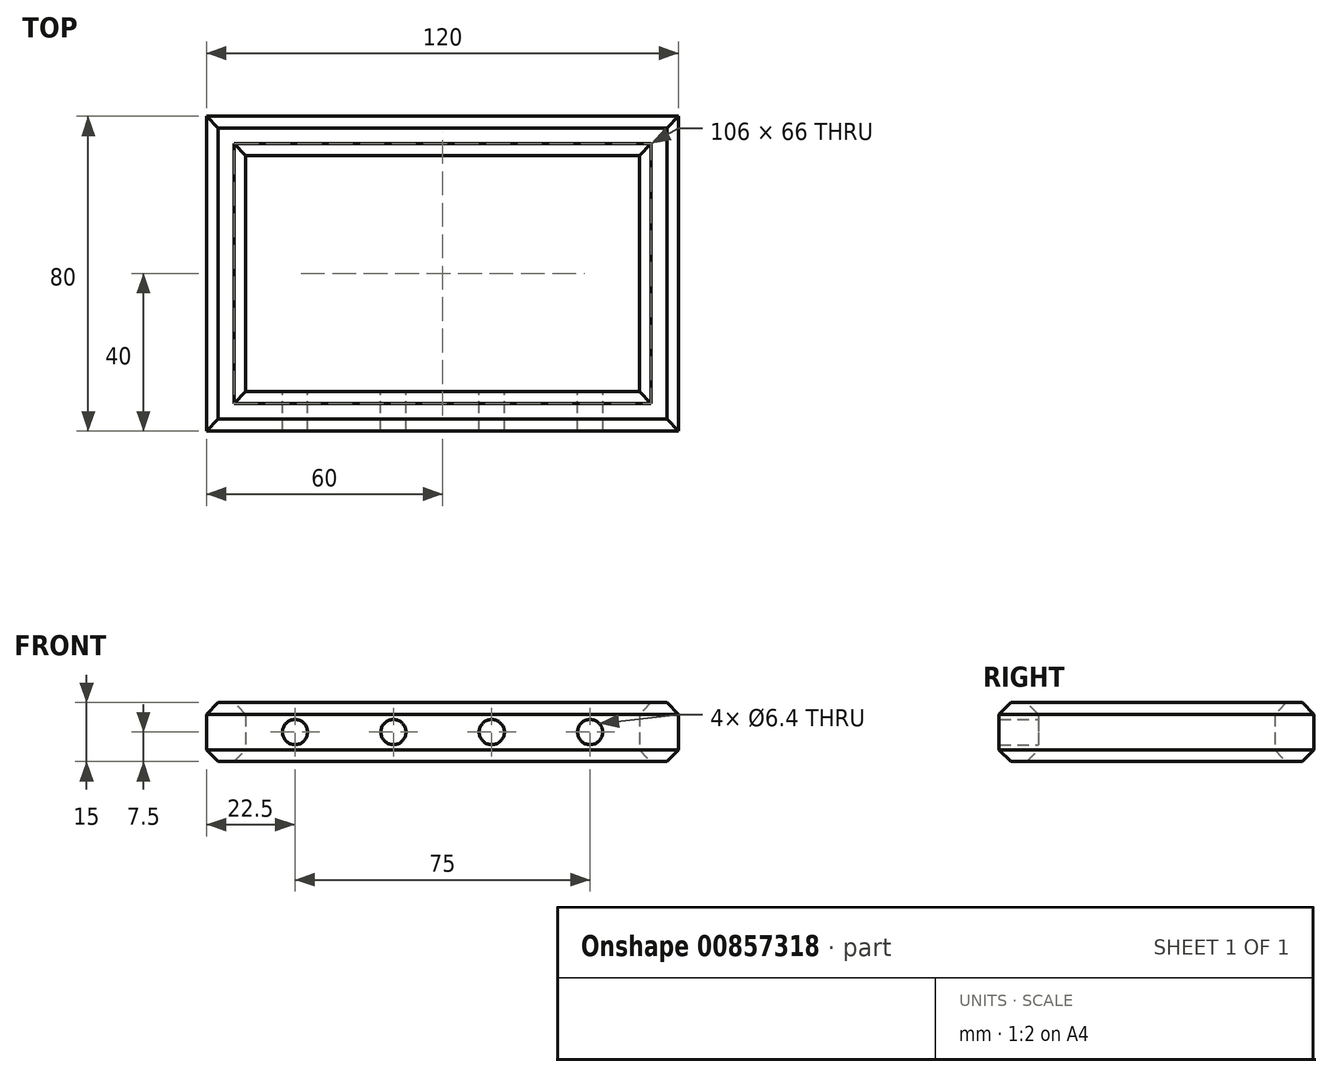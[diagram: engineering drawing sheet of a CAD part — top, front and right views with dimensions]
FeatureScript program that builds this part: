
annotation { "Feature Type Name" : "Feature", "Feature Type Description" : "" }
export const myFeature = defineFeature(function(context is Context, id is Id, definition is map)
    precondition{}
    {
        {
            var Q0;
            Q0=qCreatedBy(makeId("Top.planeOp"),FACE);
            var sketch = newSketch(context, id + "F0", { "sketchPlane" : qUnion([Q0])});
            skLineSegment(sketch, "E0", {"start": v(0, 0) * mm, "end": v(-53.05, 0) * mm, "construction": true});
            skLineSegment(sketch, "E1", {"start": v(0, 0) * mm, "end": v(0, 23.05) * mm, "construction": true});
            skLineSegment(sketch, "E2", {"start": v(0, 0) * mm, "end": v(9.55, 0) * mm, "construction": true});
            skLineSegment(sketch, "E3", {"start": v(0, 0) * mm, "end": v(0, -12.76) * mm, "construction": true});
            skLineSegment(sketch, "E4.bottom", {"start": v(0, 0) * mm, "end": v(-120, 0) * mm});
            skLineSegment(sketch, "E4.top", {"start": v(0, 80) * mm, "end": v(-120, 80) * mm});
            skLineSegment(sketch, "E4.left", {"start": v(0, 0) * mm, "end": v(0, 80) * mm});
            skLineSegment(sketch, "E4.right", {"start": v(-120, 0) * mm, "end": v(-120, 80) * mm});
            skLineSegment(sketch, "E5.bottom", {"start": v(-10, 10) * mm, "end": v(-110, 10) * mm});
            skLineSegment(sketch, "E5.top", {"start": v(-10, 70) * mm, "end": v(-110, 70) * mm});
            skLineSegment(sketch, "E5.left", {"start": v(-10, 10) * mm, "end": v(-10, 70) * mm});
            skLineSegment(sketch, "E5.right", {"start": v(-110, 10) * mm, "end": v(-110, 70) * mm});
            skSolve(sketch);
        }
        {
            var Q0;
            Q0=makeQuery(id+"F0.imprint","IMPRINT",FACE,{"disambiguationData":[TD([[makeQuery(id+"F0.imprint","IMPRINT",EDGE,{"derivedFrom":sQuery(id+"F0.wireOp",EDGE,"E4.bottom")}),-1.0]])]});
            extrude(context, id + "F1", {"entities" : qUnion([Q0]), "depth" : 15 * mm, "offsetDistance" : 25 * mm});
        }
        {
            var Q0;
            Q0=makeQuery(id+"F1.opExtrude","SWEPT_FACE",FACE,{"disambiguationData":[OSD([sQuery(id+"F0.wireOp",EDGE,"E5.bottom")])]});
            var sketch = newSketch(context, id + "F2", { "sketchPlane" : qUnion([Q0])});
            skCircle(sketch, "E6", {"center": v(72.5, 7.5) * mm, "radius": 3.2 * mm});
            skCircle(sketch, "E7", {"center": v(47.5, 7.5) * mm, "radius": 3.2 * mm});
            skLineSegment(sketch, "E8", {"start": v(74.14, 7.5) * mm, "end": v(32.95, 7.5) * mm, "construction": true});
            skLineSegment(sketch, "E9", {"start": v(60, 10.85) * mm, "end": v(60, 4.57) * mm, "construction": true});
            skCircle(sketch, "E10", {"center": v(97.5, 7.5) * mm, "radius": 3.2 * mm});
            skCircle(sketch, "E11", {"center": v(22.5, 7.5) * mm, "radius": 3.2 * mm});
            skSolve(sketch);
        }
        {
            var Q0;
            Q0=makeQuery(id+"F2.imprint","IMPRINT",FACE,{"disambiguationData":[TD([[makeQuery(id+"F2.imprint","IMPRINT",EDGE,{"derivedFrom":sQuery(id+"F2.wireOp",EDGE,"E6")}),1.0]])]});
            var Q1;
            Q1=makeQuery(id+"F2.imprint","IMPRINT",FACE,{"disambiguationData":[TD([[makeQuery(id+"F2.imprint","IMPRINT",EDGE,{"derivedFrom":sQuery(id+"F2.wireOp",EDGE,"E7")}),1.0]])]});
            var Q2;
            Q2=makeQuery(id+"F2.imprint","IMPRINT",FACE,{"disambiguationData":[TD([[makeQuery(id+"F2.imprint","IMPRINT",EDGE,{"derivedFrom":sQuery(id+"F2.wireOp",EDGE,"E10")}),1.0]])]});
            var Q3;
            Q3=makeQuery(id+"F2.imprint","IMPRINT",FACE,{"disambiguationData":[TD([[makeQuery(id+"F2.imprint","IMPRINT",EDGE,{"derivedFrom":sQuery(id+"F2.wireOp",EDGE,"E11")}),1.0]])]});
            extrude(context, id + "F3", {"entities" : qUnion([Q0, Q1, Q2, Q3]), "operationType" : NewBodyOperationType.REMOVE, "endBound" : BoundingType.THROUGH_ALL, "oppositeDirection" : true, "depth" : 25 * mm, "offsetDistance" : 25 * mm});
        }
        {
            var Q0;
            Q0=makeQuery(id+"F1.opExtrude","CAP_FACE",FACE,{"disambiguationData":[OSD([sQuery(id+"F0.wireOp",EDGE,"E4.bottom"),sQuery(id+"F0.wireOp",EDGE,"E4.top"),sQuery(id+"F0.wireOp",EDGE,"E4.left"),sQuery(id+"F0.wireOp",EDGE,"E4.right"),sQuery(id+"F0.wireOp",EDGE,"E5.bottom"),sQuery(id+"F0.wireOp",EDGE,"E5.top"),sQuery(id+"F0.wireOp",EDGE,"E5.left"),sQuery(id+"F0.wireOp",EDGE,"E5.right")])],"isStart":false});
            var Q1;
            Q1=makeQuery(id+"F1.opExtrude","CAP_FACE",FACE,{"disambiguationData":[OSD([sQuery(id+"F0.wireOp",EDGE,"E4.bottom"),sQuery(id+"F0.wireOp",EDGE,"E4.top"),sQuery(id+"F0.wireOp",EDGE,"E4.left"),sQuery(id+"F0.wireOp",EDGE,"E4.right"),sQuery(id+"F0.wireOp",EDGE,"E5.bottom"),sQuery(id+"F0.wireOp",EDGE,"E5.top"),sQuery(id+"F0.wireOp",EDGE,"E5.left"),sQuery(id+"F0.wireOp",EDGE,"E5.right")])],"isStart":true});
            chamfer(context, id + "F4", {"entities" : qUnion([Q0, Q1]), "width" : 3 * mm, "tangentPropagation" : true});
        }
    });
